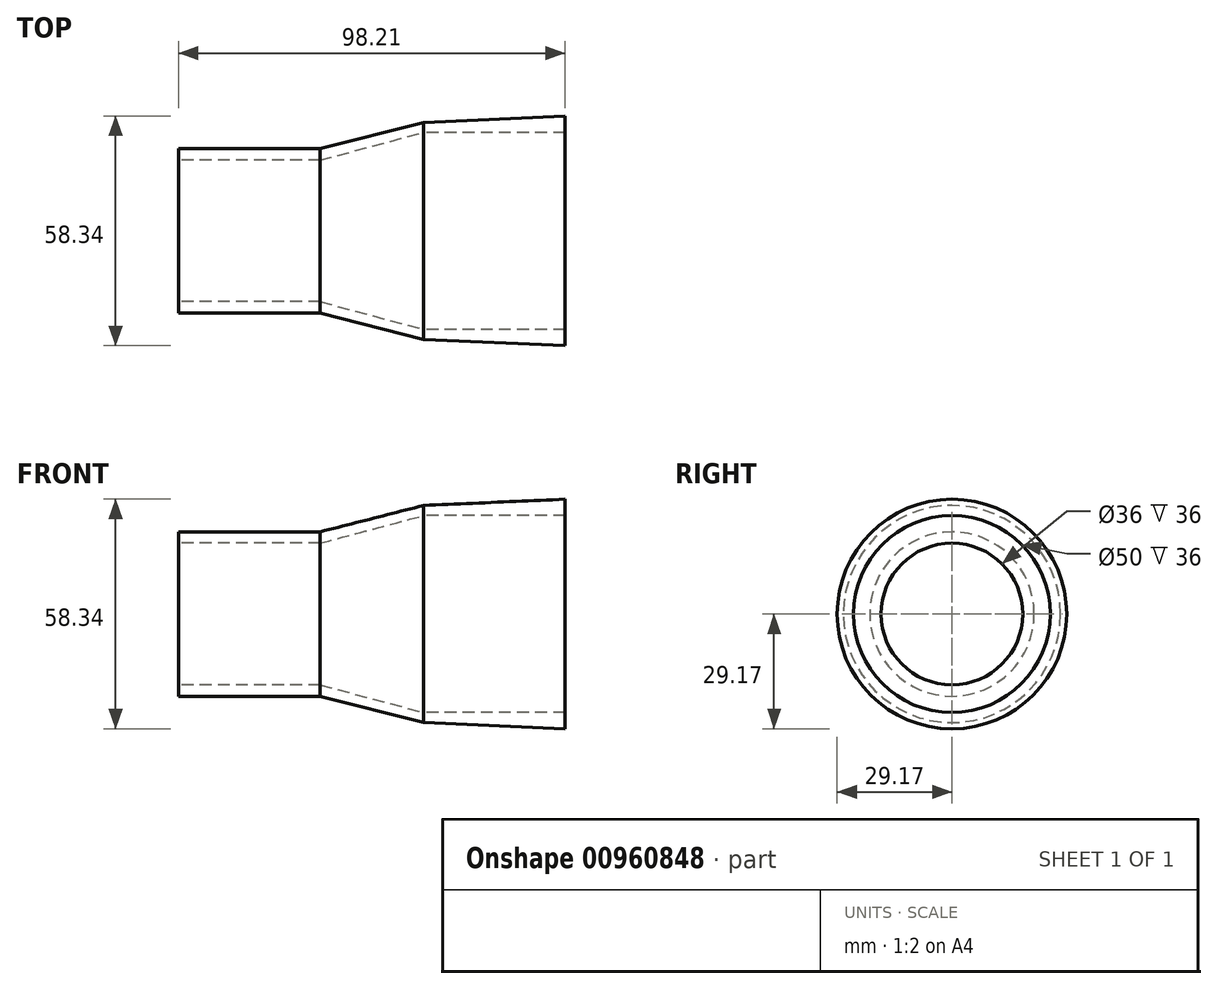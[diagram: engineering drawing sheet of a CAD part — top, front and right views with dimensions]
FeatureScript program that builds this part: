
annotation { "Feature Type Name" : "Feature", "Feature Type Description" : "" }
export const myFeature = defineFeature(function(context is Context, id is Id, definition is map)
    precondition{}
    {
        {
            var Q0;
            Q0=qCreatedBy(makeId("Top.planeOp"),FACE);
            var sketch = newSketch(context, id + "F0", { "sketchPlane" : qUnion([Q0])});
            skLineSegment(sketch, "E0", {"start": v(40.7, 29.24) * mm, "end": v(40.7, 25) * mm});
            skLineSegment(sketch, "E1", {"start": v(40.7, 25) * mm, "end": v(4.7, 25) * mm});
            skLineSegment(sketch, "E2", {"start": v(4.7, 25) * mm, "end": v(-21.5, 18) * mm});
            skLineSegment(sketch, "E3", {"start": v(-21.5, 18) * mm, "end": v(-57.5, 18) * mm});
            skLineSegment(sketch, "E4", {"start": v(-57.5, 18) * mm, "end": v(-57.5, 20.88) * mm});
            skLineSegment(sketch, "E5", {"start": v(-57.5, 20.88) * mm, "end": v(-21.5, 20.88) * mm});
            skLineSegment(sketch, "E6", {"start": v(-21.5, 20.88) * mm, "end": v(4.7, 27.58) * mm});
            skLineSegment(sketch, "E7", {"start": v(4.7, 27.58) * mm, "end": v(42.43, 29.24) * mm});
            skLineSegment(sketch, "E8", {"start": v(-43.34, 0) * mm, "end": v(39.1, 0) * mm, "construction": true});
            skLineSegment(sketch, "E9", {"start": v(22.7, 25) * mm, "end": v(22.7, 0) * mm, "construction": true});
            skPoint(sketch, "E10", {"position": v(-31.2, 18) * mm});
            skLineSegment(sketch, "E11", {"start": v(-31.2, 18) * mm, "end": v(-31.2, 0) * mm, "construction": true});
            skSolve(sketch);
        }
        {
            var Q0;
            {var subQ0=sQuery(id+"F0.wireOp",EDGE,"E1");Q0=makeQuery(id+"F0.imprint","IMPRINT",FACE,{"disambiguationData":[TD([[makeQuery(id+"F0.imprint","IMPRINT",EDGE,{"derivedFrom":subQ0}),-1.0]])]});}
            var Q1;
            Q1=sQuery(id+"F0.wireOp",EDGE,"E8");
            revolve(context, id + "F1", {"surfaceOperationType" : NewSurfaceOperationType.NEW, "entities" : qUnion([Q0]), "axis" : qUnion([Q1]), "revolveType" : RevolveType.FULL});
        }
    });
